# Revit family: 60420
name_source: partatom
category: Pipe Accessories
revit_build: Autodesk Revit 2018 (Build: 20170223_1515(x64)
units: mm (PartAtom-declared; Revit-internal decimal feet)

## family parameters
Always vertical = Yes
Cut with Voids When Loaded = No
Part Type = Normal
Round Connector Dimension = Use Diameter
Shared = No
Work Plane-Based = No

## types (5) — shared parameters
Adresse = 7, RUE RACINE - 92542 MONTROUGE CEDEX FRANCE
LC = 15 mm  [stored 0.0492126 ft]
Lien CCTP = http://www.prestodatashare.com
Lien fiche produit = http://www.prestodatashare.com
Manufacturer = LES ROBINETS PRESTO S.A.
PC = 30 mm  [stored 0.0984252 ft]
Perte de charge = 0.0 Pa
URL = http://www.prestodatashare.com
URL Fabricant = http://www.prestodatashare.com

## per-type parameters (varying)
| type | Description | Edition number | Flux | Fonction | Hauteur | Largeur | Lien notice d'utilisation | Matériau | Polantis code | Product data url | Profondeur | Reference | Résistance en pression statique |
| 28619 PRESTO MITIGEUR TEMPORISE PRESTO 4000"S" BOUTON CHROME+FLEXIBLES PEX - DEBIT 2L/MIN | Mitigeur mono-commande temporisé sur plage. De type Presto 4000 S® réf. 28619 ou techniquement équivalent. Avec mécanisme à rubis auto nettoyé par fil frein, limiteur de débit intégré (1,9 l/mn), sécurité S® interdisant le blocage en écoulement continu, limitation de la température maximale par butée ajustable. Bouton de commande en laiton chromé. Avec flexibles PEX et robinets d’arrêt filtres. | 0 | 0.0 L/s | Pression d'utilisation recommandée :
- 1 à 5 bars

Débit :
- 1,9 l/mn avec sprayer limiteur de débit intégré
- Dispositif anti-coup de bélier
- Brise-jet : anti-vandalisme et anti-bouchage

Durée d'écoulement :
- 15 secondes +/- 5 secondes

Alimentation hydraulique :
- G 3/8'' (12x17)

Matière et couleur de finition :
- Bouton-poussoir en laiton chromé

Résistance thermique :
- Ce robinet résiste à une température de 75°C durant 30 minutes dans le cadre de chocs thermiques

Sécurité :
- Limitation de la température maximale par butée ajustable
- Système S® interdisant le blocage en écoulement continu

Livré avec :
- 2 Robinets d'arrêt MM 3/8'' (12x17)
- 2 Joints filtre
- 2 Flexibles PEX avec clapets anti-retour NF et écrous tournants
- 1 Bride de fixation
- 1 Joint de bride
- 1 Ecrou de fixation

Normes / Agréments :
- Classe acoustique I
- Résistance au brouillard salin 200 H conformément à la norme NF ISO 9227 essai DSS
- Corps en laiton chromé conforme aux normes NF EN1982, EN12164, EN 12165 | 144 mm | 50 mm |  | <By Category> | PRE050002d-FR |  | 166 mm | 28619 |  |
| 28617 PRESTO MITIGEUR TEMPORISE PRESTO 4000"S" BOUTON CHROME+FLEXIBLES PEX SANS RA | Mitigeur NF mono-commande temporisé sur plage. De type Presto 4000 S® réf. 28617 ou techniquement équivalent. Avec mécanisme à rubis auto nettoyé par fil frein, régulateur de débit intégré (3l/min), sécurité S® interdisant le blocage en écoulement continu, limitation de la température maximale par butée ajustable. Bouton de commande en laiton chromé. Avec flexibles PEX et joints  filtres. | 0 | 0.1 L/s | Pression d'utilisation recommandée :
- 1 à 5 bars

Débit :
- 3 l/mn avec limiteur de débit intégré
- Dispositif anti-coup de bélier
- Brise-jet : anti-vandalisme et anti-bouchage

Durée d'écoulement :
- 15 secondes ± 5 secondes

Alimentation hydraulique :
- G 3/8'' (12x17)

Matière et couleur de finition :
- Bouton-poussoir en laiton chromé

Résistance thermique :
- Ce robinet résiste à une température de 75°C durant 30 minutes dans le cadre de chocs thermiques

Sécurité :
- Limitation de la température maximale par butée ajustable
- Système S® interdisant le blocage en écoulement continu

Livré avec :
- 2 Joints filtre
- 2 Flexibles PEX avec clapets anti-retour NF et écrous tournants
- 1 Bride de fixation
- 1 Joint de bride
- 1 Ecrou de fixation

Normes / Agréments :
- Résistance au brouillard salin 200 H conformément à la norme NF ISO 9227 essai DSS
- Corps en laiton chromé conforme aux normes NF EN1982, EN12164, EN 12165 | 144 mm | 50 mm |  | <By Category> | PRE050002c-FR |  | 166 mm | 28617 |  |
| 28610 PRESTO MITIGEUR TEMPORISE PRESTO 4000"S" BOUTON CHROME+FLEXIBLES PEX | Mitigeur NF mono-commande temporisé sur plage. De type Presto 4000 S® réf. 28610 ou techniquement équivalent. Avec mécanisme à rubis auto nettoyé par fil frein, régulateur de débit intégré (3l/min), sécurité S® interdisant le blocage en écoulement continu, limitation de la température maximale par butée ajustable. Bouton de commande en laiton chromé. Avec flexibles PEX et robinets d’arrêt filtres. | 0 | 0.1 L/s | Pression d'utilisation recommandée :
- 1 à 5 bars

Débit :
- 3 l/mn avec limiteur de débit intégré
- Dispositif anti-coup de bélier
- Brise-jet : anti-vandalisme et anti-bouchage

Durée d'écoulement :
- 15 secondes ± 5 secondes

Alimentation hydraulique :
- G 3/8'' (12x17)

Matière et couleur de finition :
- Bouton-poussoir en laiton chromé

Résistance thermique :
- Ce robinet résiste à une température de 75°C durant 30 minutes dans le cadre de chocs thermiques

Sécurité :
- Limitation de la température maximale par butée ajustable
- Système S® interdisant le blocage en écoulement continu

Livré avec :
- 2 Robinets d'arrêt MM 3/8'' (12x17)
- 2 Joints filtre
- 2 Flexibles PEX avec clapets anti-retour NF et écrous tournants
- 1 Bride de fixation
- 1 Joint de bride
- 1 Ecrou de fixation

Normes / Agréments :
- Classe acoustique I
- Résistance au brouillard salin 200 H conformément à la norme NF ISO 9227 essai DSS
- Corps en laiton chromé conforme aux normes NF EN1982, EN12164, EN12165 | 144 mm | 50 mm |  | <By Category> | PRE050002b-FR |  | 166 mm | 28610 |  |
| 28442 PRESTO MITIGEUR TEMPORISE PRESTO 4000"S" BOUTON NOIR + FLEXIBLES PEX | Mitigeur NF mono-commande temporisé sur plage. De type Presto 4000 S® réf. 28442 ou techniquement équivalent. Avec mécanisme à rubis auto nettoyé par fil frein, régulateur de débit intégré (3l/min), sécurité S® interdisant le blocage en écoulement continu, limitation de la température maximale par butée ajustable. Bouton de commande en polyacétal noir. Avec flexibles PEX et robinets d’arrêt filtres. | 0 | 0.1 L/s | Pression d'utilisation recommandée :
- 1 à 5 bars

Débit :
- 3 l/mn avec limiteur de débit intégré
- Dispositif anti-coup de bélier
- Brise-jet : anti-vandalisme et anti-bouchage

Durée d'écoulement :
- 15 secondes ± 5 secondes

Alimentation hydraulique :
- G 3/8'' (12x17)

Matière et couleur de finition :
- Bouton-poussoir noir en polyacétal

Résistance thermique :
- Ce robinet résiste à une température de 75°C durant 30 minutes dans le cadre de chocs thermiques

Sécurité :
- Limitation de la température maximale par butée ajustable
- Système S® interdisant le blocage en écoulement continu

Livré avec :
- 2 Robinets d'arrêt MM 3/8'' (12x17)
- 2 Joints filtre
- 2 Flexibles PEX avec clapets anti-retour NF et écrous tournants
- 1 Bride de fixation
- 1 Joint de bride
- 1 Ecrou de fixation

Normes / Agréments :
- Classe acoustique I
- Résistance au brouillard salin 200 H conformément à la norme NF ISO 9227 essai DSS
- Corps en laiton chromé conforme aux normes NF EN1982, EN12164, EN12165 | 144 mm | 50 mm |  | <By Category> | PRE050002a-FR |  | 166 mm | 28442 |  |
| 60420 PRESTO Hanging shower seat |  | 1 | 0.1 L/s | Pression d'utilisation recommandée :
- 1 à 5 bars

Débit :
- 3 l/mn avec limiteur de débit intégré
- Dispositif anti-coup de bélier
- Brise-jet : anti-vandalisme et anti-bouchage

Durée d'écoulement :
- 15 secondes ± 5 secondes

Alimentation hydraulique :
- G 3/8'' (12x17)

Matière et couleur de finition :
- Bouton-poussoir noir en polyacétal

Résistance thermique :
- Ce robinet résiste à une température de 75°C durant 30 minutes dans le cadre de chocs thermiques

Sécurité :
- Limitation de la température maximale par butée ajustable
- Système S® interdisant le blocage en écoulement continu

Livré avec :
- 2 Joints filtre
- 2 Flexibles PEX avec clapets anti-retour NF et écrous tournants
- 1 Bride de fixation
- 1 Joint de bride
- 1 Ecrou de fixation

Normes / Agréments :
- Résistance au brouillard salin 200 H conformément à la norme NF ISO 9227 essai DSS
- Corps en laiton chromé conforme aux normes NF EN1982, EN12164, EN 12165 | 450 mm  [stored 1.47638 ft] | 400 mm  [stored 1.31234 ft] | http://www.prestodatashare.com | nylon blanc | PRE080033 | https://www.bimobject.com | 515 mm  [stored 1.68963 ft] | 60420 | 150 kg (testé à plus de 200 kg) |

note: column(s) folded — value = type name in every type: Model

note: [stored X ft] marks values corroborated as IEEE doubles in the binary element streams (Revit-internal decimal feet)
